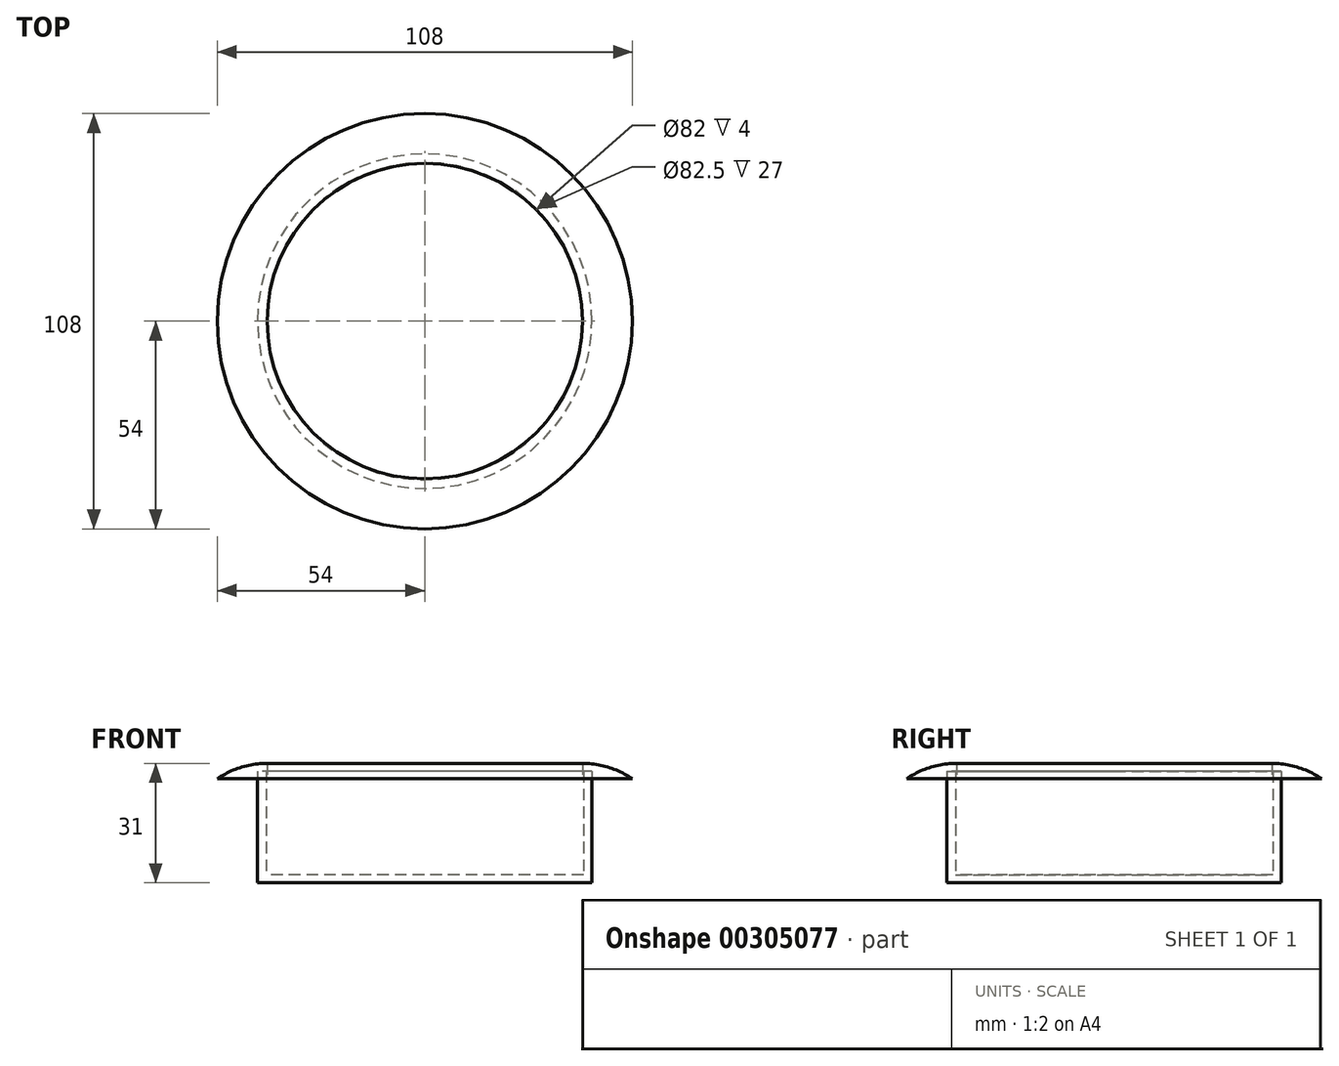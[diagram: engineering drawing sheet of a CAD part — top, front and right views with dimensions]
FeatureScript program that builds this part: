
annotation { "Feature Type Name" : "Feature", "Feature Type Description" : "" }
export const myFeature = defineFeature(function(context is Context, id is Id, definition is map)
    precondition{}
    {
        {
            var Q0;
            Q0=qCreatedBy(makeId("Top.planeOp"),FACE);
            var sketch = newSketch(context, id + "F0", { "sketchPlane" : qUnion([Q0])});
            skCircle(sketch, "E0", {"center": v(0, 0) * mm, "radius": 41.25 * mm});
            skCircle(sketch, "E1", {"center": v(0, 0) * mm, "radius": 43.5 * mm});
            skSolve(sketch);
        }
        {
            var Q0;
            Q0=makeQuery(id+"F0.imprint","IMPRINT",FACE,{"disambiguationData":[TD([[makeQuery(id+"F0.imprint","IMPRINT",EDGE,{"derivedFrom":sQuery(id+"F0.wireOp",EDGE,"E0")}),-1.0]])]});
            extrude(context, id + "F1", {"entities" : qUnion([Q0]), "depth" : 29 * mm});
        }
        {
            var Q0;
            Q0=makeQuery(id+"F0.imprint","IMPRINT",FACE,{"disambiguationData":[TD([[makeQuery(id+"F0.imprint","IMPRINT",EDGE,{"derivedFrom":sQuery(id+"F0.wireOp",EDGE,"E0")}),1.0]])]});
            extrude(context, id + "F2", {"entities" : qUnion([Q0]), "operationType" : NewBodyOperationType.ADD, "depth" : 2 * mm});
        }
        {
            var Q0;
            Q0=makeQuery(id+"F1.opExtrude","CAP_FACE",FACE,{"disambiguationData":[OSD([sQuery(id+"F0.wireOp",EDGE,"E0"),sQuery(id+"F0.wireOp",EDGE,"E1")])],"isStart":false});
            var sketch = newSketch(context, id + "F3", { "sketchPlane" : qUnion([Q0])});
            skCircle(sketch, "E2", {"center": v(0, 0) * mm, "radius": 54 * mm});
            skSolve(sketch);
        }
        {
            var Q0;
            Q0 = qSketchRegion(id + "F3", true);
            extrude(context, id + "F4", {"entities" : qUnion([Q0]), "endBound" : BoundingType.SYMMETRIC, "oppositeDirection" : true, "depth" : 4 * mm});
        }
        {
            var Q0;
            Q0=makeQuery(id+"F2.opExtrude","CAP_FACE",FACE,{"disambiguationData":[OSD([sQuery(id+"F0.wireOp",EDGE,"E0")])],"isStart":false});
            var sketch = newSketch(context, id + "F5", { "sketchPlane" : qUnion([Q0])});
            skCircle(sketch, "E3", {"center": v(0, 0) * mm, "radius": 41 * mm});
            skSolve(sketch);
        }
        {
            var Q0;
            Q0=makeQuery(id+"F5.imprint","IMPRINT",FACE,{"disambiguationData":[TD([[makeQuery(id+"F5.imprint","IMPRINT",EDGE,{"derivedFrom":sQuery(id+"F5.wireOp",EDGE,"E3")}),1.0]])]});
            extrude(context, id + "F6", {"entities" : qUnion([Q0]), "operationType" : NewBodyOperationType.REMOVE, "endBound" : BoundingType.THROUGH_ALL, "depth" : 30 * mm});
        }
        {
            var Q0;
            Q0=makeQuery(id+"F4.opExtrude","CAP_EDGE",EDGE,{"disambiguationData":[OSD([sQuery(id+"F3.wireOp",EDGE,"E2")])],"isStart":true});
            fillet(context, id + "F7", {"entities" : qUnion([Q0]), "radius" : 23 * mm, "tangentPropagation" : true, "allowEdgeOverflow" : false});
        }
    });
